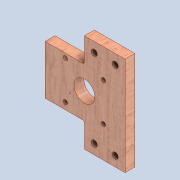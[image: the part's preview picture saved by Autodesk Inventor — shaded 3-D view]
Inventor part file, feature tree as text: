
AUTODESK INVENTOR PART (.ipt)
format: ipt  version: 2020 (Build 240168000, 168)  size: 175,104 bytes
history: native  units: mm
features: sketch x4, extrude x3, hole x1, pattern_linear x1, fillet x1
ambient origin geometry x8: Origin, YZ Plane, XZ Plane, XY Plane, X Axis, Y Axis, Z Axis, Center Point
bodies: Solid1 (feature_tree)
feature tree (10):
  extrude  "Extrusion1"  Depth=40.0mm
  extrude  "Extrusion5"  Depth=20.0mm
  extrude  "Extrusion6"  Depth=33.0mm
  hole  "Hole1"  [1 undecoded]
  pattern_linear  "Rectangular Pattern1"  Spacing1=33.0mm  [1 undecoded]
  fillet  "Fillet1"  Radius=39.0mm
  sketch  "Sketch1"  dims[d0=65.0mm d1=40.0mm]
  sketch  "Sketch5"  dims[d2=8.0mm d3=0.0mm d22=20.0mm]
  sketch  "Sketch6"  dims[d23=20.0mm d24=33.0mm]
  sketch  "Sketch7"  dims[d25=10.0mm d26=0.0mm d29=31.0mm d30=33.0mm d31=39.0mm d32=3.5mm d33=17.0mm d34=10.0mm d35=0.0mm d36=8.0mm d37=8.0mm d38=8.0mm d39=17.0mm d40=8.0mm d41=64.0mm d42=5.0mm d43=6.0mm d44=4.0mm d45=2.0mm d46=90.0deg d47=8.0mm d48=20.594885mm d49=20.0mm d51=64.0mm d52=20.0mm d54=17.0mm d55=1.5mm]
note: 2 required parameter values undecoded (feature->parameter linkage not recoverable at this tier; creation-order binding heuristic only, values carry confidence <= 0.55)
